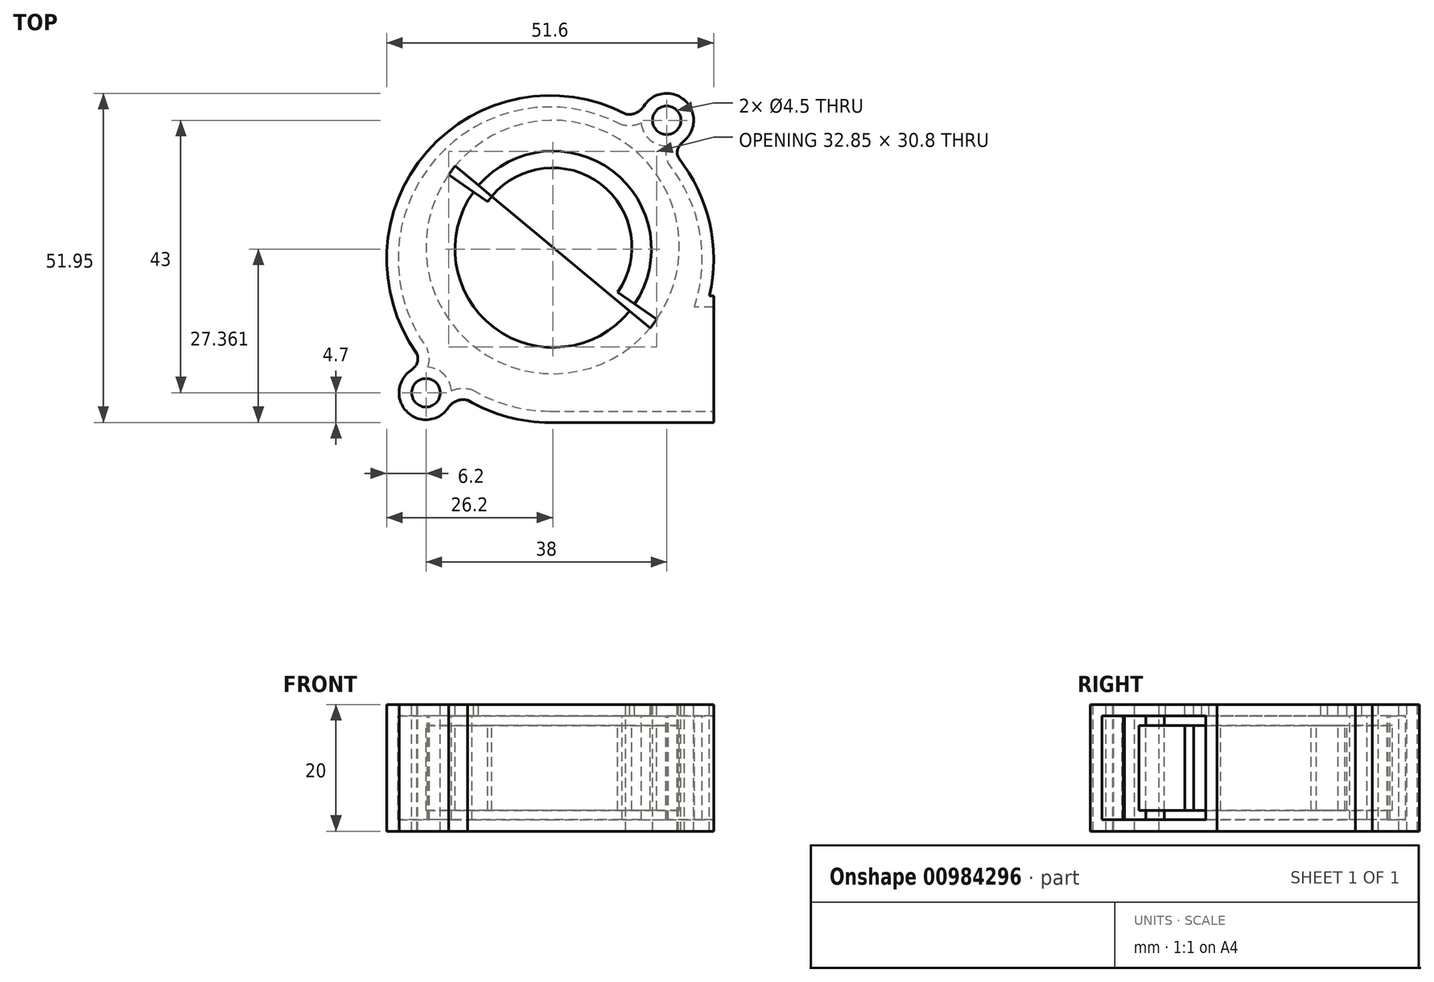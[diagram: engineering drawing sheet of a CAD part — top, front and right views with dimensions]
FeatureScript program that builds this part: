
annotation { "Feature Type Name" : "Feature", "Feature Type Description" : "" }
export const myFeature = defineFeature(function(context is Context, id is Id, definition is map)
    precondition{}
    {
        {
            var Q0;
            Q0=qCreatedBy(makeId("Top.planeOp"),FACE);
            var sketch = newSketch(context, id + "F0", { "sketchPlane" : qUnion([Q0])});
            skCircle(sketch, "E0", {"center": v(0.09, -0.35) * mm, "radius": 15.5 * mm});
            skCircle(sketch, "E1", {"center": v(-0.4, -1.9) * mm, "radius": 25.8 * mm});
            skLineSegment(sketch, "E2", {"start": v(-0.4, -27.7) * mm, "end": v(25.4, -27.7) * mm});
            skLineSegment(sketch, "E3", {"start": v(25.4, -27.7) * mm, "end": v(25.4, -7.7) * mm});
            skLineSegment(sketch, "E4", {"start": v(25.4, -7.7) * mm, "end": v(24.74, -7.7) * mm});
            skCircle(sketch, "E5", {"center": v(-20, -23) * mm, "radius": 2.25 * mm});
            skCircle(sketch, "E6", {"center": v(18, 20) * mm, "radius": 2.25 * mm});
            skArc(sketch, "E7", {"start": v(20.82, 16.82) * mm, "mid": v(20.73, 23.25) * mm, "end": v(14.38, 22.23) * mm});
            skFitSpline(sketch, "E8", {"points": [v(20.82, 16.82) * mm, v(19.82, 14.13) * mm], "startDerivative": vector(-1.7, -1.47) * mm, "endDerivative": vector(1.58, -4.22) * mm});
            skFitSpline(sketch, "E9", {"points": [v(14.38, 22.23) * mm, v(11.51, 20.98) * mm], "startDerivative": vector(-1.2, -1.9) * mm, "endDerivative": vector(-4.5, 0.79) * mm});
            skArc(sketch, "E10", {"start": v(-22.5, -19.57) * mm, "mid": v(-22.9, -26.11) * mm, "end": v(-16.4, -25.25) * mm});
            skFitSpline(sketch, "E11", {"points": [v(-22.5, -19.57) * mm, v(-21.42, -16.86) * mm], "startDerivative": vector(1.81, 1.33) * mm, "endDerivative": vector(-1.52, 4.5) * mm});
            skFitSpline(sketch, "E12", {"points": [v(-16.4, -25.25) * mm, v(-13.43, -24.17) * mm], "startDerivative": vector(1.16, 1.93) * mm, "endDerivative": vector(4.4, -0.97) * mm});
            skSolve(sketch);
        }
        {
            var Q0;
            Q0=makeQuery(id+"F0.imprint","IMPRINT",FACE,{"disambiguationData":[TD([[makeQuery(id+"F0.imprint","IMPRINT",EDGE,{"derivedFrom":sQuery(id+"F0.wireOp",EDGE,"E0")}),-1.0]])]});
            var Q1;
            Q1=makeQuery(id+"F0.imprint","IMPRINT",FACE,{"disambiguationData":[TD([[makeQuery(id+"F0.imprint","IMPRINT",EDGE,{"derivedFrom":sQuery(id+"F0.wireOp",EDGE,"E6")}),-1.0]])]});
            var Q2;
            Q2=makeQuery(id+"F0.imprint","IMPRINT",FACE,{"disambiguationData":[TD([[makeQuery(id+"F0.imprint","IMPRINT",EDGE,{"derivedFrom":sQuery(id+"F0.wireOp",EDGE,"E5")}),-1.0]])]});
            var Q3;
            {var subQ0=sQuery(id+"F0.wireOp",EDGE,"E2");Q3=makeQuery(id+"F0.imprint","IMPRINT",FACE,{"disambiguationData":[TD([[makeQuery(id+"F0.imprint","IMPRINT",EDGE,{"derivedFrom":subQ0}),1.0]])]});}
            var Q4;
            Q4=makeQuery(id+"F0.imprint","IMPRINT",FACE,{"disambiguationData":[TD([[makeQuery(id+"F0.imprint","IMPRINT",EDGE,{"derivedFrom":sQuery(id+"F0.wireOp",EDGE,"bf398d43-aba3-4df9-bdcc-5d3f5d1128fe")}),-1.0]])]});
            var Q5;
            Q5=makeQuery(id+"F0.imprint","IMPRINT",FACE,{"disambiguationData":[TD([[makeQuery(id+"F0.imprint","IMPRINT",EDGE,{"derivedFrom":sQuery(id+"F0.wireOp",EDGE,"bf398d43-aba3-4df9-bdcc-5d3f5d1128fe")}),1.0]])]});
            var Q6;
            Q6=makeQuery(id+"F0.imprint","IMPRINT",FACE,{"disambiguationData":[TD([[makeQuery(id+"F0.imprint","IMPRINT",EDGE,{"derivedFrom":sQuery(id+"F0.wireOp",EDGE,"E0")}),1.0]])]});
            extrude(context, id + "F1", {"entities" : qUnion([Q0, Q1, Q2, Q3, Q4, Q5, Q6]), "oppositeDirection" : true, "depth" : 20 * mm, "offsetDistance" : 25 * mm});
        }
        {
            var Q0;
            Q0=makeQuery(id+"F1.opExtrude","SWEPT_FACE",FACE,{"disambiguationData":[OSD([sQuery(id+"F0.wireOp",EDGE,"E3")])]});
            shell(context, id + "F2", {"entities" : qUnion([Q0]), "thickness" : 1.8 * mm});
        }
        {
            var Q0;
            Q0=makeQuery(id+"F0.imprint","IMPRINT",FACE,{"disambiguationData":[TD([[makeQuery(id+"F0.imprint","IMPRINT",EDGE,{"derivedFrom":sQuery(id+"F0.wireOp",EDGE,"E0")}),1.0]])]});
            extrude(context, id + "F3", {"entities" : qUnion([Q0]), "operationType" : NewBodyOperationType.REMOVE, "oppositeDirection" : true, "depth" : 1.8 * mm, "offsetDistance" : 25 * mm});
        }
        {
            var Q0;
            Q0=qCreatedBy(makeId("Top.planeOp"),FACE);
            var sketch = newSketch(context, id + "F4", { "sketchPlane" : qUnion([Q0])});
            skCircle(sketch, "E13", {"center": v(0, 0) * mm, "radius": 20 * mm});
            skCircle(sketch, "E14", {"center": v(0, 0) * mm, "radius": 12.5 * mm});
            skLineSegment(sketch, "E15", {"start": v(-16.43, 11.4) * mm, "end": v(16.43, -11.4) * mm});
            skLineSegment(sketch, "E16", {"start": v(15.37, -12.8) * mm, "end": v(-15.37, 12.8) * mm});
            skSolve(sketch);
        }
        {
            var Q0;
            {var subQ0=sQuery(id+"F4.wireOp",EDGE,"E15");var subQ1=sQuery(id+"F4.wireOp",EDGE,"E13");var subQ2=makeQuery(id+"F4.imprint","INTERSECT",VERTEX,{"disambiguationData":[OD(1.0)],"derivedFrom":[subQ1,subQ0]});Q0=makeQuery(id+"F4.imprint","IMPRINT",FACE,{"disambiguationData":[TD([[makeQuery(id+"F4.imprint","IMPRINT",EDGE,{"disambiguationData":[TD([[subQ2,-1.0]])],"derivedFrom":subQ1}),1.0]])]});}
            var Q1;
            {var subQ0=sQuery(id+"F4.wireOp",EDGE,"E15");var subQ1=sQuery(id+"F4.wireOp",EDGE,"E13");var subQ2=makeQuery(id+"F4.imprint","INTERSECT",VERTEX,{"disambiguationData":[OD(0.0)],"derivedFrom":[subQ1,subQ0]});Q1=makeQuery(id+"F4.imprint","IMPRINT",FACE,{"disambiguationData":[TD([[makeQuery(id+"F4.imprint","IMPRINT",EDGE,{"disambiguationData":[TD([[subQ2,1.0]])],"derivedFrom":subQ1}),1.0]])]});}
            var Q2;
            {var subQ0=sQuery(id+"F4.wireOp",EDGE,"E15");var subQ1=sQuery(id+"F4.wireOp",EDGE,"E13");var subQ2=makeQuery(id+"F4.imprint","INTERSECT",VERTEX,{"disambiguationData":[OD(0.0)],"derivedFrom":[subQ1,subQ0]});Q2=makeQuery(id+"F4.imprint","IMPRINT",FACE,{"disambiguationData":[TD([[makeQuery(id+"F4.imprint","IMPRINT",EDGE,{"disambiguationData":[TD([[subQ2,-1.0]])],"derivedFrom":subQ1}),1.0]])]});}
            var Q3;
            {var subQ0=sQuery(id+"F4.wireOp",EDGE,"E15");var subQ1=sQuery(id+"F4.wireOp",EDGE,"E13");var subQ2=makeQuery(id+"F4.imprint","INTERSECT",VERTEX,{"disambiguationData":[OD(1.0)],"derivedFrom":[subQ1,subQ0]});Q3=makeQuery(id+"F4.imprint","IMPRINT",FACE,{"disambiguationData":[TD([[makeQuery(id+"F4.imprint","IMPRINT",EDGE,{"disambiguationData":[TD([[subQ2,1.0]])],"derivedFrom":subQ1}),1.0]])]});}
            var Q4;
            {var subQ0=sQuery(id+"F4.wireOp",EDGE,"E15");var subQ1=sQuery(id+"F4.wireOp",EDGE,"E14");var subQ2=makeQuery(id+"F4.imprint","INTERSECT",VERTEX,{"disambiguationData":[OD(0.0)],"derivedFrom":[subQ1,subQ0]});Q4=makeQuery(id+"F4.imprint","IMPRINT",FACE,{"disambiguationData":[TD([[makeQuery(id+"F4.imprint","IMPRINT",EDGE,{"disambiguationData":[TD([[subQ2,-1.0]])],"derivedFrom":subQ1}),1.0]])]});}
            var Q5;
            {var subQ0=sQuery(id+"F4.wireOp",EDGE,"E15");var subQ1=sQuery(id+"F4.wireOp",EDGE,"E14");var subQ2=makeQuery(id+"F4.imprint","INTERSECT",VERTEX,{"disambiguationData":[OD(0.0)],"derivedFrom":[subQ1,subQ0]});Q5=makeQuery(id+"F4.imprint","IMPRINT",FACE,{"disambiguationData":[TD([[makeQuery(id+"F4.imprint","IMPRINT",EDGE,{"disambiguationData":[TD([[subQ2,1.0]])],"derivedFrom":subQ1}),1.0]])]});}
            var Q6;
            {var subQ0=sQuery(id+"F4.wireOp",EDGE,"E16");var subQ1=sQuery(id+"F4.wireOp",EDGE,"E14");var subQ2=makeQuery(id+"F4.imprint","INTERSECT",VERTEX,{"disambiguationData":[OD(1.0)],"derivedFrom":[subQ1,subQ0]});Q6=makeQuery(id+"F4.imprint","IMPRINT",FACE,{"disambiguationData":[TD([[makeQuery(id+"F4.imprint","IMPRINT",EDGE,{"disambiguationData":[TD([[subQ2,-1.0]])],"derivedFrom":subQ1}),1.0]])]});}
            var Q7;
            {var subQ0=sQuery(id+"F4.wireOp",EDGE,"E16");var subQ1=sQuery(id+"F4.wireOp",EDGE,"E14");var subQ2=makeQuery(id+"F4.imprint","INTERSECT",VERTEX,{"disambiguationData":[OD(0.0)],"derivedFrom":[subQ1,subQ0]});Q7=makeQuery(id+"F4.imprint","IMPRINT",FACE,{"disambiguationData":[TD([[makeQuery(id+"F4.imprint","IMPRINT",EDGE,{"disambiguationData":[TD([[subQ2,1.0]])],"derivedFrom":subQ1}),1.0]])]});}
            extrude(context, id + "F5", {"entities" : qUnion([Q0, Q1, Q2, Q3, Q4, Q5, Q6, Q7]), "oppositeDirection" : true, "depth" : 16.7 * mm, "offsetDistance" : 25 * mm, "hasSecondDirection" : true, "secondDirectionOppositeDirection" : true, "secondDirectionDepth" : 3.3 * mm});
        }
        {
            var Q0;
            {var subQ0=sQuery(id+"F4.wireOp",EDGE,"E15");var subQ1=sQuery(id+"F4.wireOp",EDGE,"E13");var subQ2=makeQuery(id+"F4.imprint","INTERSECT",VERTEX,{"disambiguationData":[OD(0.0)],"derivedFrom":[subQ1,subQ0]});Q0=makeQuery(id+"F4.imprint","IMPRINT",FACE,{"disambiguationData":[TD([[makeQuery(id+"F4.imprint","IMPRINT",EDGE,{"disambiguationData":[TD([[subQ2,1.0]])],"derivedFrom":subQ1}),1.0]])]});}
            var Q1;
            {var subQ0=sQuery(id+"F4.wireOp",EDGE,"E15");var subQ1=sQuery(id+"F4.wireOp",EDGE,"E13");var subQ2=makeQuery(id+"F4.imprint","INTERSECT",VERTEX,{"disambiguationData":[OD(1.0)],"derivedFrom":[subQ1,subQ0]});Q1=makeQuery(id+"F4.imprint","IMPRINT",FACE,{"disambiguationData":[TD([[makeQuery(id+"F4.imprint","IMPRINT",EDGE,{"disambiguationData":[TD([[subQ2,1.0]])],"derivedFrom":subQ1}),1.0]])]});}
            var Q2;
            Q2=makeQuery(id+"F5.opExtrude","CAP_FACE",FACE,{"disambiguationData":[OSD([sQuery(id+"F4.wireOp",EDGE,"E13")])],"isStart":false});
            var Q3;
            Q3=makeQuery(id+"F5.opExtrude","SWEPT_BODY",BODY,{"disambiguationData":[OSD([sQuery(id+"F4.wireOp",EDGE,"E13")])]});
            extrude(context, id + "F6", {"entities" : qUnion([Q0, Q1]), "operationType" : NewBodyOperationType.REMOVE, "endBound" : BoundingType.UP_TO_SURFACE, "oppositeDirection" : true, "depth" : 25 * mm, "endBoundEntityFace" : qUnion([Q2]), "endBoundEntityBody" : qUnion([Q3]), "offsetDistance" : 25 * mm});
        }
    });
